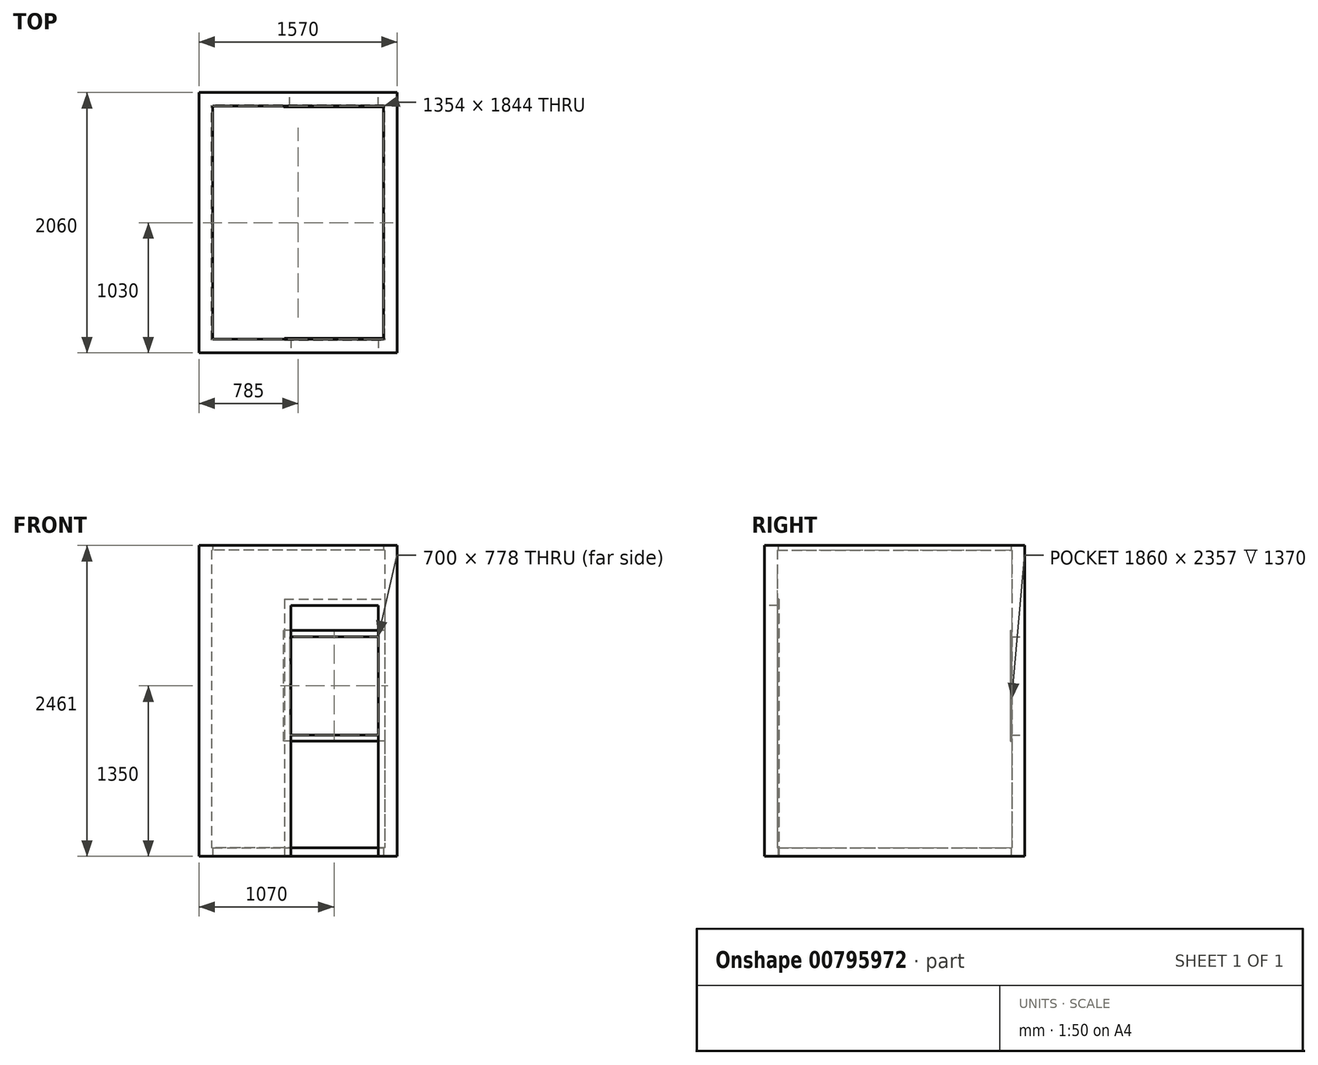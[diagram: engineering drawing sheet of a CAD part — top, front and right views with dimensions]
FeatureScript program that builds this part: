
annotation { "Feature Type Name" : "Feature", "Feature Type Description" : "" }
export const myFeature = defineFeature(function(context is Context, id is Id, definition is map)
    precondition{}
    {
        {
            var Q0;
            Q0=qCreatedBy(makeId("Top.planeOp"),FACE);
            var sketch = newSketch(context, id + "F0", { "sketchPlane" : qUnion([Q0])});
            skLineSegment(sketch, "E0.bottom", {"start": v(0, 0) * mm, "end": v(-1370, 0) * mm});
            skLineSegment(sketch, "E0.top", {"start": v(0, 1860) * mm, "end": v(-1370, 1860) * mm});
            skLineSegment(sketch, "E0.left", {"start": v(0, 0) * mm, "end": v(0, 1860) * mm});
            skLineSegment(sketch, "E0.right", {"start": v(-1370, 0) * mm, "end": v(-1370, 1860) * mm});
            skLineSegment(sketch, "E1.0", {"start": v(100, 1960) * mm, "end": v(-1470, 1960) * mm});
            skLineSegment(sketch, "E1.1", {"start": v(100, -100) * mm, "end": v(100, 1960) * mm});
            skLineSegment(sketch, "E1.2", {"start": v(100, -100) * mm, "end": v(-1470, -100) * mm});
            skLineSegment(sketch, "E1.3", {"start": v(-1470, -100) * mm, "end": v(-1470, 1960) * mm});
            skSolve(sketch);
        }
        {
            var Q0;
            Q0=makeQuery(id+"F0.imprint","IMPRINT",FACE,{"disambiguationData":[TD([[makeQuery(id+"F0.imprint","IMPRINT",EDGE,{"derivedFrom":sQuery(id+"F0.wireOp",EDGE,"E0.bottom")}),1.0]])]});
            extrude(context, id + "F1", {"entities" : qUnion([Q0]), "depth" : 2425 * mm, "offsetDistance" : 25 * mm});
        }
        {
            var Q0;
            Q0=makeQuery(id+"F1.opExtrude","SWEPT_FACE",FACE,{"disambiguationData":[OSD([sQuery(id+"F0.wireOp",EDGE,"E0.bottom")])]});
            var sketch = newSketch(context, id + "F2", { "sketchPlane" : qUnion([Q0])});
            skLineSegment(sketch, "E2.bottom", {"start": v(793, 0) * mm, "end": v(0, 0) * mm});
            skLineSegment(sketch, "E2.top", {"start": v(793, 2036) * mm, "end": v(0, 2036) * mm});
            skLineSegment(sketch, "E2.left", {"start": v(0, 0) * mm, "end": v(0, 2036) * mm});
            skLineSegment(sketch, "E2.right", {"start": v(793, 2036) * mm, "end": v(793, 0) * mm});
            skSolve(sketch);
        }
        {
            var Q0;
            Q0 = qSketchRegion(id + "F2", true);
            extrude(context, id + "F3", {"entities" : qUnion([Q0]), "operationType" : NewBodyOperationType.ADD, "depth" : 14 * mm, "offsetDistance" : 25 * mm});
        }
        {
            var Q0;
            Q0=makeQuery(id+"F1.opExtrude","SWEPT_FACE",FACE,{"disambiguationData":[OSD([sQuery(id+"F0.wireOp",EDGE,"E1.2")])]});
            var sketch = newSketch(context, id + "F4", { "sketchPlane" : qUnion([Q0])});
            skLineSegment(sketch, "E3.bottom", {"start": v(-743, 0) * mm, "end": v(-50, 0) * mm});
            skLineSegment(sketch, "E3.top", {"start": v(-743, 1986) * mm, "end": v(-50, 1986) * mm});
            skLineSegment(sketch, "E3.left", {"start": v(-743, 0) * mm, "end": v(-743, 1986) * mm});
            skLineSegment(sketch, "E3.right", {"start": v(-50, 0) * mm, "end": v(-50, 1986) * mm});
            skSolve(sketch);
        }
        {
            var Q0;
            Q0=makeQuery(id+"F4.imprint","IMPRINT",FACE,{"disambiguationData":[TD([[makeQuery(id+"F4.imprint","IMPRINT",EDGE,{"derivedFrom":sQuery(id+"F4.wireOp",EDGE,"E3.bottom")}),-1.0]])]});
            extrude(context, id + "F5", {"entities" : qUnion([Q0]), "operationType" : NewBodyOperationType.REMOVE, "endBound" : BoundingType.UP_TO_NEXT, "oppositeDirection" : true, "depth" : 25 * mm, "offsetDistance" : 25 * mm});
        }
        {
            var Q0;
            Q0=makeQuery(id+"F1.opExtrude","SWEPT_FACE",FACE,{"disambiguationData":[OSD([sQuery(id+"F0.wireOp",EDGE,"E0.top")])]});
            var sketch = newSketch(context, id + "F6", { "sketchPlane" : qUnion([Q0])});
            skLineSegment(sketch, "E4.bottom", {"start": v(0, 911) * mm, "end": v(-800, 911) * mm});
            skLineSegment(sketch, "E4.top", {"start": v(0, 1789) * mm, "end": v(-800, 1789) * mm});
            skLineSegment(sketch, "E4.left", {"start": v(0, 911) * mm, "end": v(0, 1789) * mm});
            skLineSegment(sketch, "E4.right", {"start": v(-800, 911) * mm, "end": v(-800, 1789) * mm});
            skSolve(sketch);
        }
        {
            var Q0;
            Q0=makeQuery(id+"F6.imprint","IMPRINT",FACE,{"disambiguationData":[TD([[makeQuery(id+"F6.imprint","IMPRINT",EDGE,{"derivedFrom":sQuery(id+"F6.wireOp",EDGE,"E4.bottom")}),-1.0]])]});
            extrude(context, id + "F7", {"entities" : qUnion([Q0]), "operationType" : NewBodyOperationType.ADD, "depth" : 14 * mm, "offsetDistance" : 25 * mm});
        }
        {
            var Q0;
            Q0=makeQuery(id+"F1.opExtrude","SWEPT_FACE",FACE,{"disambiguationData":[OSD([sQuery(id+"F0.wireOp",EDGE,"E1.0")])]});
            var sketch = newSketch(context, id + "F8", { "sketchPlane" : qUnion([Q0])});
            skLineSegment(sketch, "E5.bottom", {"start": v(50, 1739) * mm, "end": v(750, 1739) * mm});
            skLineSegment(sketch, "E5.top", {"start": v(50, 961) * mm, "end": v(750, 961) * mm});
            skLineSegment(sketch, "E5.left", {"start": v(50, 1739) * mm, "end": v(50, 961) * mm});
            skLineSegment(sketch, "E5.right", {"start": v(750, 1739) * mm, "end": v(750, 961) * mm});
            skSolve(sketch);
        }
        {
            var Q0;
            Q0=makeQuery(id+"F8.imprint","IMPRINT",FACE,{"disambiguationData":[TD([[makeQuery(id+"F8.imprint","IMPRINT",EDGE,{"derivedFrom":sQuery(id+"F8.wireOp",EDGE,"E5.bottom")}),-1.0]])]});
            extrude(context, id + "F9", {"entities" : qUnion([Q0]), "operationType" : NewBodyOperationType.REMOVE, "endBound" : BoundingType.UP_TO_NEXT, "oppositeDirection" : true, "depth" : 25 * mm, "offsetDistance" : 25 * mm});
        }
        {
            var Q0;
            Q0=makeQuery(id+"F3.boolean.opBoolean","MERGE",FACE,{"derivedFrom":[makeQuery(id+"F1.opExtrude","CAP_FACE",FACE,{"disambiguationData":[OSD([sQuery(id+"F0.wireOp",EDGE,"E0.bottom"),sQuery(id+"F0.wireOp",EDGE,"E0.top"),sQuery(id+"F0.wireOp",EDGE,"E0.left"),sQuery(id+"F0.wireOp",EDGE,"E0.right"),sQuery(id+"F0.wireOp",EDGE,"E1.0"),sQuery(id+"F0.wireOp",EDGE,"E1.1"),sQuery(id+"F0.wireOp",EDGE,"E1.2"),sQuery(id+"F0.wireOp",EDGE,"E1.3")])],"isStart":true}),makeQuery(id+"F3.opExtrude","SWEPT_FACE",FACE,{"disambiguationData":[OSD([sQuery(id+"F2.wireOp",EDGE,"E2.bottom")])]})]});
            var sketch = newSketch(context, id + "F10", { "sketchPlane" : qUnion([Q0])});
            skLineSegment(sketch, "E6.bottom", {"start": v(-1361, -9) * mm, "end": v(-743, -9) * mm});
            skLineSegment(sketch, "E6.top", {"start": v(-1361, -1851) * mm, "end": v(-9, -1851) * mm});
            skLineSegment(sketch, "E6.left", {"start": v(-1361, -9) * mm, "end": v(-1361, -1851) * mm});
            skLineSegment(sketch, "E7.bottom", {"start": v(-1370, 0) * mm, "end": v(-743, 0) * mm});
            skLineSegment(sketch, "E7.top", {"start": v(-1370, -1860) * mm, "end": v(0, -1860) * mm});
            skLineSegment(sketch, "E7.left", {"start": v(-1370, 0) * mm, "end": v(-1370, -1860) * mm});
            skLineSegment(sketch, "E8", {"start": v(-743, 0) * mm, "end": v(-743, -9) * mm});
            skLineSegment(sketch, "E9", {"start": v(-9, -14) * mm, "end": v(-9, -14) * mm});
            skLineSegment(sketch, "E10", {"start": v(-9, -14) * mm, "end": v(0, -14) * mm});
            skLineSegment(sketch, "E11", {"start": v(0, -14) * mm, "end": v(0, -1860) * mm});
            skLineSegment(sketch, "E12", {"start": v(-9, -14) * mm, "end": v(-9, -1851) * mm});
            skSolve(sketch);
        }
        {
            var Q0;
            Q0 = qSketchRegion(id + "F10", true);
            extrude(context, id + "F11", {"entities" : qUnion([Q0]), "operationType" : NewBodyOperationType.ADD, "oppositeDirection" : true, "depth" : 68 * mm, "offsetDistance" : 25 * mm});
        }
        {
            var Q0;
            Q0=makeQuery(id+"F1.opExtrude","CAP_FACE",FACE,{"disambiguationData":[OSD([sQuery(id+"F0.wireOp",EDGE,"E0.bottom"),sQuery(id+"F0.wireOp",EDGE,"E0.top"),sQuery(id+"F0.wireOp",EDGE,"E0.left"),sQuery(id+"F0.wireOp",EDGE,"E0.right"),sQuery(id+"F0.wireOp",EDGE,"E1.0"),sQuery(id+"F0.wireOp",EDGE,"E1.1"),sQuery(id+"F0.wireOp",EDGE,"E1.2"),sQuery(id+"F0.wireOp",EDGE,"E1.3")])],"isStart":false});
            var sketch = newSketch(context, id + "F12", { "sketchPlane" : qUnion([Q0])});
            skLineSegment(sketch, "E13.0", {"start": v(-8, 1852) * mm, "end": v(-1362, 1852) * mm});
            skLineSegment(sketch, "E13.1", {"start": v(-8, 8) * mm, "end": v(-8, 1852) * mm});
            skLineSegment(sketch, "E13.2", {"start": v(-8, 8) * mm, "end": v(-1362, 8) * mm});
            skLineSegment(sketch, "E13.3", {"start": v(-1362, 8) * mm, "end": v(-1362, 1852) * mm});
            skLineSegment(sketch, "E14.bottom", {"start": v(-1470, 1960) * mm, "end": v(100, 1960) * mm});
            skLineSegment(sketch, "E14.top", {"start": v(-1470, -100) * mm, "end": v(100, -100) * mm});
            skLineSegment(sketch, "E14.left", {"start": v(-1470, 1960) * mm, "end": v(-1470, -100) * mm});
            skLineSegment(sketch, "E14.right", {"start": v(100, 1960) * mm, "end": v(100, -100) * mm});
            skSolve(sketch);
        }
        {
            var Q0;
            Q0 = qSketchRegion(id + "F12", true);
            extrude(context, id + "F13", {"entities" : qUnion([Q0]), "operationType" : NewBodyOperationType.ADD, "depth" : 36 * mm, "offsetDistance" : 25 * mm});
        }
    });
